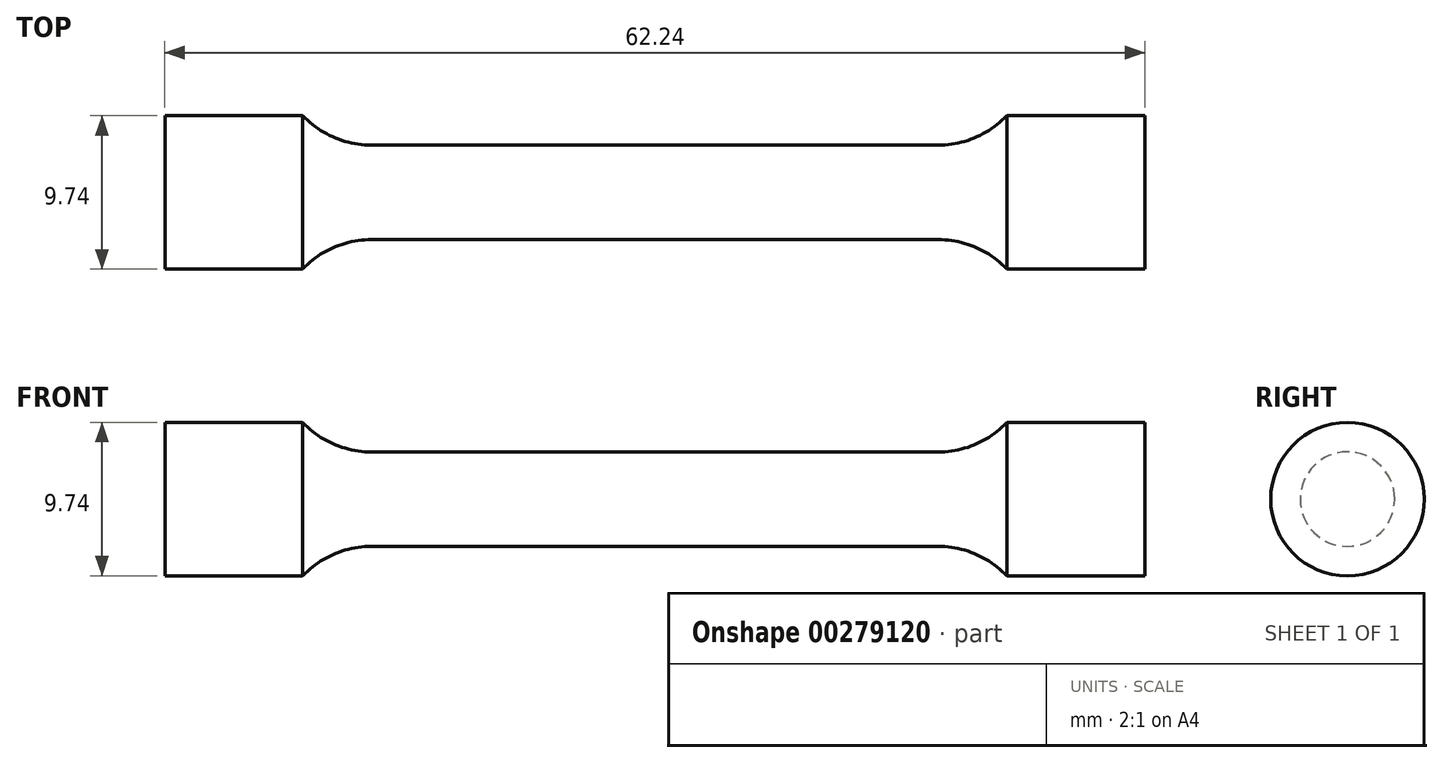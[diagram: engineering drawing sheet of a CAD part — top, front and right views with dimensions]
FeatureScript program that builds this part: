
annotation { "Feature Type Name" : "Feature", "Feature Type Description" : "" }
export const myFeature = defineFeature(function(context is Context, id is Id, definition is map)
    precondition{}
    {
        {
            var Q0;
            Q0=qCreatedBy(makeId("Front.planeOp"),FACE);
            var sketch = newSketch(context, id + "F0", { "sketchPlane" : qUnion([Q0])});
            skLineSegment(sketch, "E0", {"start": v(0, 3) * mm, "end": v(18, 3) * mm});
            skArc(sketch, "E1", {"start": v(18, 3) * mm, "mid": v(20.37, 3.49) * mm, "end": v(22.36, 4.87) * mm});
            skLineSegment(sketch, "E2", {"start": v(22.36, 4.87) * mm, "end": v(31.12, 4.87) * mm});
            skLineSegment(sketch, "E3", {"start": v(31.12, 4.87) * mm, "end": v(31.12, 0) * mm});
            skLineSegment(sketch, "E4", {"start": v(31.12, 0) * mm, "end": v(0, 0) * mm});
            skLineSegment(sketch, "E5.MirrorCS", {"start": v(0, 3) * mm, "end": v(-18, 3) * mm});
            skLineSegment(sketch, "E6.MirrorCS", {"start": v(-31.12, 0) * mm, "end": v(0, 0) * mm});
            skLineSegment(sketch, "E7.MirrorCS", {"start": v(-22.36, 4.87) * mm, "end": v(-31.12, 4.87) * mm});
            skLineSegment(sketch, "E8.MirrorCS", {"start": v(-31.12, 4.87) * mm, "end": v(-31.12, 0) * mm});
            skArc(sketch, "E9.MirrorCS", {"start": v(-18, 3) * mm, "mid": v(-20.37, 3.49) * mm, "end": v(-22.36, 4.87) * mm});
            skSolve(sketch);
        }
        {
            var Q0;
            Q0 = qSketchRegion(id + "F0", true);
            var Q1;
            Q1=sQuery(id+"F0.wireOp",EDGE,"E6.MirrorCS");
            revolve(context, id + "F1", {"entities" : qUnion([Q0]), "axis" : qUnion([Q1]), "revolveType" : RevolveType.FULL});
        }
    });
